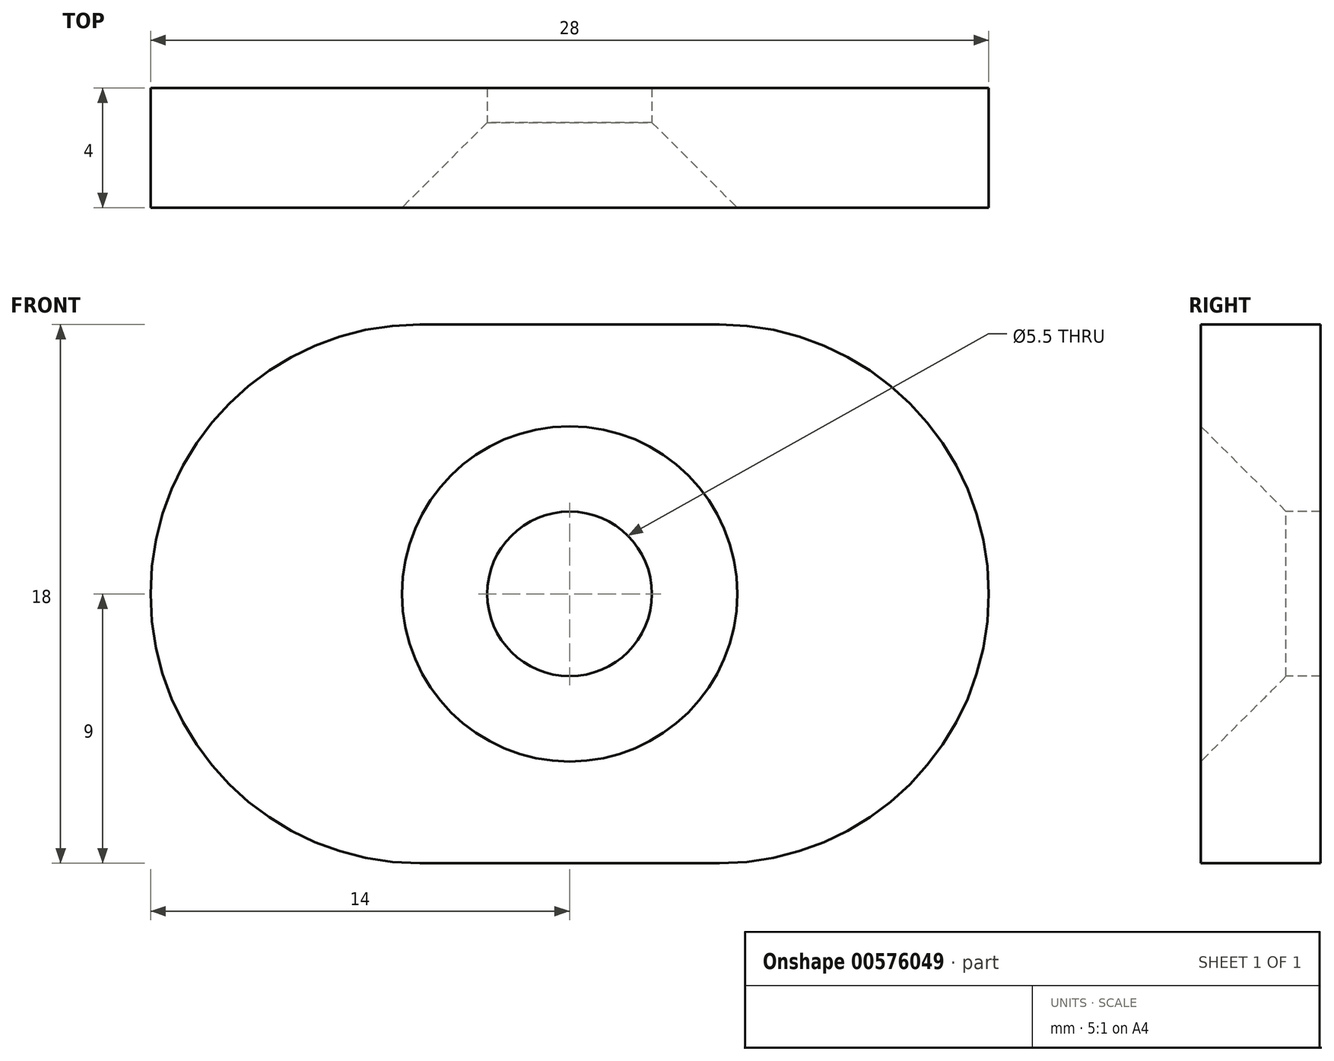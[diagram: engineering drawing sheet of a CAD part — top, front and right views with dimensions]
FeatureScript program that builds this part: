
annotation { "Feature Type Name" : "Feature", "Feature Type Description" : "" }
export const myFeature = defineFeature(function(context is Context, id is Id, definition is map)
    precondition{}
    {
        {
            var Q0;
            Q0=qCreatedBy(makeId("Front.planeOp"),FACE);
            var sketch = newSketch(context, id + "F0", { "sketchPlane" : qUnion([Q0])});
            skLineSegment(sketch, "E0.bottom", {"start": v(-5, -9) * mm, "end": v(5, -9) * mm});
            skLineSegment(sketch, "E0.top", {"start": v(-5, 9) * mm, "end": v(5, 9) * mm});
            skLineSegment(sketch, "E0.left", {"start": v(-14, 0) * mm, "end": v(-14, 0) * mm});
            skLineSegment(sketch, "E0.right", {"start": v(14, 0) * mm, "end": v(14, 0) * mm});
            skPoint(sketch, "E1.visualSharp", {"position": v(14, 9) * mm});
            skArc(sketch, "E1.filletArc", {"start": v(14, 0) * mm, "mid": v(11.36, 6.36) * mm, "end": v(5, 9) * mm});
            skPoint(sketch, "E2.visualSharp", {"position": v(14, -9) * mm});
            skArc(sketch, "E2.filletArc", {"start": v(5, -9) * mm, "mid": v(11.36, -6.36) * mm, "end": v(14, 0) * mm});
            skPoint(sketch, "E3.visualSharp", {"position": v(-14, 9) * mm});
            skArc(sketch, "E3.filletArc", {"start": v(-5, 9) * mm, "mid": v(-11.36, 6.36) * mm, "end": v(-14, 0) * mm});
            skPoint(sketch, "E4.visualSharp", {"position": v(-14, -9) * mm});
            skArc(sketch, "E4.filletArc", {"start": v(-14, 0) * mm, "mid": v(-11.36, -6.36) * mm, "end": v(-5, -9) * mm});
            skSolve(sketch);
        }
        {
            var Q0;
            Q0=makeQuery(id+"F0.imprint","IMPRINT",FACE,{"disambiguationData":[TD([[makeQuery(id+"F0.imprint","IMPRINT",EDGE,{"derivedFrom":sQuery(id+"F0.wireOp",EDGE,"E0.bottom")}),1.0]])]});
            extrude(context, id + "F1", {"entities" : qUnion([Q0]), "depth" : 4 * mm, "offsetDistance" : 25 * mm});
        }
        {
            var Q0;
            Q0=makeQuery(id+"F1.opExtrude","CAP_FACE",FACE,{"disambiguationData":[OSD([sQuery(id+"F0.wireOp",EDGE,"E0.bottom"),sQuery(id+"F0.wireOp",EDGE,"E0.top"),sQuery(id+"F0.wireOp",EDGE,"E1.filletArc"),sQuery(id+"F0.wireOp",EDGE,"E2.filletArc"),sQuery(id+"F0.wireOp",EDGE,"E3.filletArc"),sQuery(id+"F0.wireOp",EDGE,"E4.filletArc")])],"isStart":false});
            var sketch = newSketch(context, id + "F2", { "sketchPlane" : qUnion([Q0])});
            skPoint(sketch, "E5.0", {"position": v(0, 0) * mm});
            skSolve(sketch);
        }
        {
            var Q0;
            Q0=sQuery(id+"F2.wireOp",VERTEX,"E5.0");
            var Q1;
            Q1=makeQuery(id+"F1.opExtrude","SWEPT_BODY",BODY,{"disambiguationData":[OSD([sQuery(id+"F0.wireOp",EDGE,"E0.bottom"),sQuery(id+"F0.wireOp",EDGE,"E0.top"),sQuery(id+"F0.wireOp",EDGE,"E1.filletArc"),sQuery(id+"F0.wireOp",EDGE,"E2.filletArc"),sQuery(id+"F0.wireOp",EDGE,"E3.filletArc"),sQuery(id+"F0.wireOp",EDGE,"E4.filletArc")])]});
            hole(context, id + "F3", {"style" : HoleStyle.C_SINK, "endStyle" : HoleEndStyle.THROUGH, "standardTappedOrClearance" : lookupTablePath({ "standard" : "ISO", "fit" : "Normal", "size" : "M5", "type" : "Clearance" }), "standardBlindInLast" : lookupTablePath({ "fit" : "Standard", "standard" : "ISO", "size" : "M5", "type" : "Clearance" }), "holeDiameter" : 5.5 * mm, "cSinkDiameter" : 11.2 * mm, "cSinkAngle" : 90 * degree, "isTappedThrough" : true, "tappedDepth" : 12 * mm, "tapClearance" : 3, "locations" : qUnion([Q0]), "scope" : qUnion([Q1]), "majorDiameter" : 5 * mm});
        }
    });
